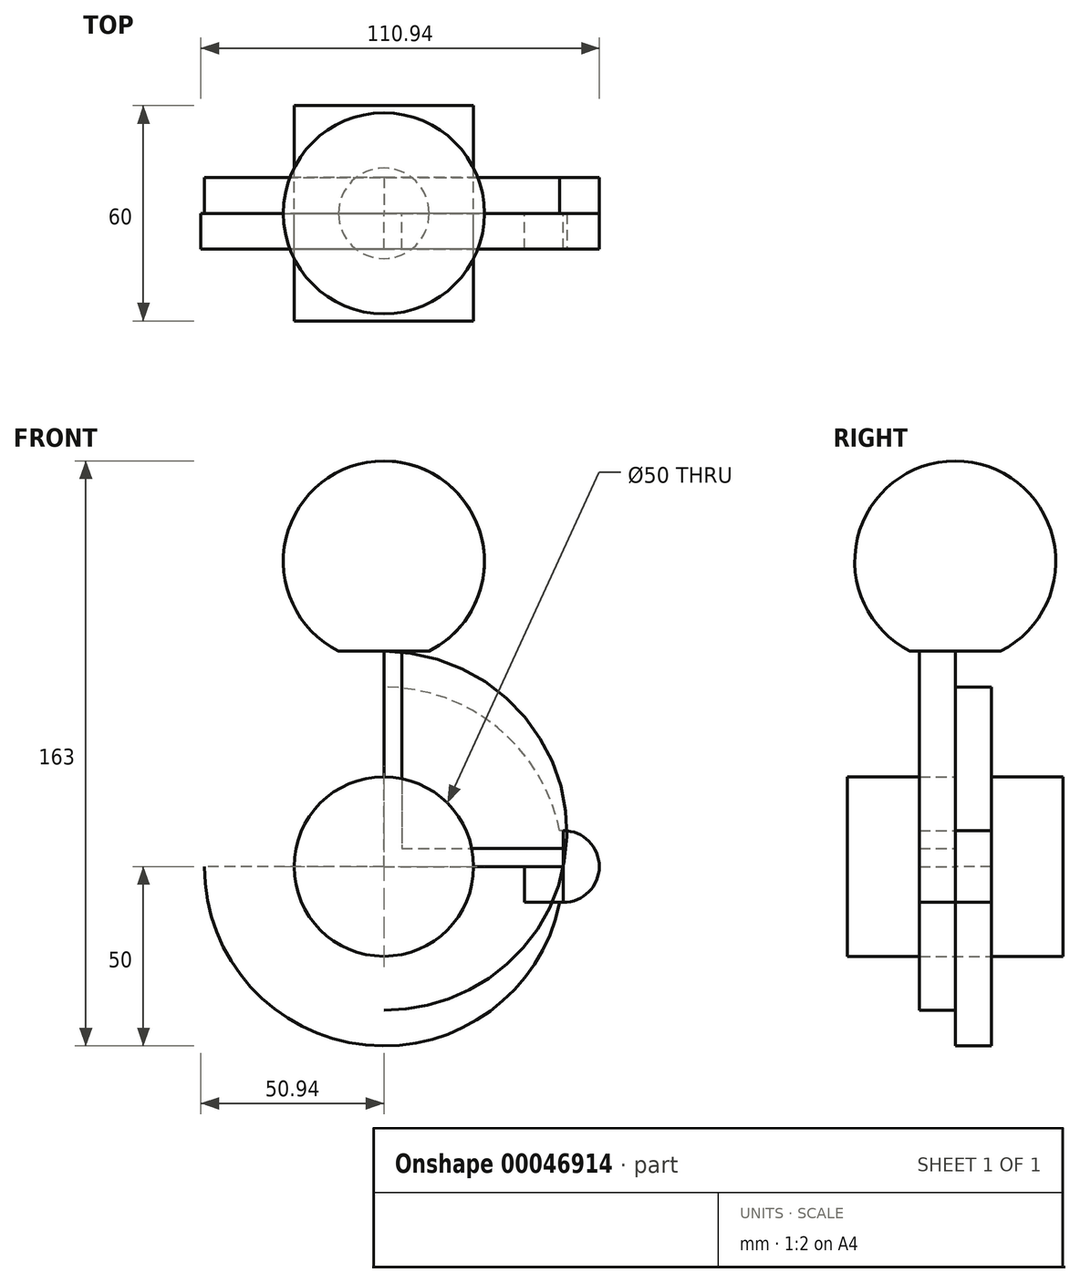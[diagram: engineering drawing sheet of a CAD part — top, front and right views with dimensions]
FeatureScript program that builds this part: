
annotation { "Feature Type Name" : "Feature", "Feature Type Description" : "" }
export const myFeature = defineFeature(function(context is Context, id is Id, definition is map)
    precondition{}
    {
        {
            var Q0;
            Q0=qCreatedBy(makeId("Front.planeOp"),FACE);
            var sketch = newSketch(context, id + "F0", { "sketchPlane" : qUnion([Q0])});
            skArc(sketch, "E0", {"start": v(49, 9.95) * mm, "mid": v(31.64, 38.71) * mm, "end": v(0, 50) * mm});
            skArc(sketch, "E1", {"start": v(49, -9.95) * mm, "mid": v(60, 0) * mm, "end": v(49, 9.95) * mm});
            skLineSegment(sketch, "E2.bottom", {"start": v(0, 0) * mm, "end": v(-50, 0) * mm});
            skLineSegment(sketch, "E2.left", {"start": v(0, 0) * mm, "end": v(0, 50) * mm});
            skArc(sketch, "E3.trimOffspring", {"start": v(-50, 0) * mm, "mid": v(-5, -49.75) * mm, "end": v(49, -9.95) * mm});
            skSolve(sketch);
        }
        {
            var Q0;
            Q0=makeQuery(id+"F0.imprint","IMPRINT",FACE,{"disambiguationData":[TD([[makeQuery(id+"F0.imprint","IMPRINT",EDGE,{"derivedFrom":sQuery(id+"F0.wireOp",EDGE,"E0")}),1.0]])]});
            extrude(context, id + "F1", {"entities" : qUnion([Q0]), "oppositeDirection" : true, "depth" : 10 * mm});
        }
        {
            var Q0;
            Q0=qCreatedBy(makeId("Front.planeOp"),FACE);
            var sketch = newSketch(context, id + "F2", { "sketchPlane" : qUnion([Q0])});
            skLineSegment(sketch, "E4", {"start": v(25, 43.3) * mm, "end": v(29.33, 50.8) * mm, "construction": true});
            skLineSegment(sketch, "E5", {"start": v(0, 50) * mm, "end": v(0, 60) * mm, "construction": true});
            skLineSegment(sketch, "E6", {"start": v(43.3, 25) * mm, "end": v(47.63, 27.5) * mm, "construction": true});
            skPoint(sketch, "E7", {"position": v(50, 0) * mm});
            skLineSegment(sketch, "E8", {"start": v(43.3, -25) * mm, "end": v(38.97, -22.5) * mm, "construction": true});
            skLineSegment(sketch, "E9", {"start": v(25, -43.3) * mm, "end": v(20.67, -35.8) * mm, "construction": true});
            skLineSegment(sketch, "E10", {"start": v(0, -50) * mm, "end": v(0, -40) * mm, "construction": true});
            skFitSpline(sketch, "E11", {"points": [v(0, 60) * mm, v(29.33, 50.8) * mm, v(47.63, 27.5) * mm, v(50, 0) * mm, v(38.97, -22.5) * mm, v(20.67, -35.8) * mm, v(0, -40) * mm], "startDerivative": vector(175.41, 0) * mm, "endDerivative": vector(-141.48, 0) * mm});
            skFitSpline(sketch, "E12.MirrorCS", {"points": [v(0, 60) * mm, v(-29.33, 50.8) * mm, v(-47.63, 27.5) * mm, v(-50, 0) * mm, v(-38.97, -22.5) * mm, v(-20.67, -35.8) * mm, v(0, -40) * mm], "startDerivative": vector(-175.41, 0) * mm, "endDerivative": vector(141.48, 0) * mm});
            skCircle(sketch, "E13", {"center": v(0, 0) * mm, "radius": 25 * mm});
            skSolve(sketch);
        }
        {
            var Q0;
            Q0 = qSketchRegion(id + "F2", true);
            extrude(context, id + "F3", {"entities" : qUnion([Q0]), "depth" : 10 * mm});
        }
        {
            var Q0;
            Q0=qCreatedBy(makeId("Front.planeOp"),FACE);
            var sketch = newSketch(context, id + "F4", { "sketchPlane" : qUnion([Q0])});
            skCircle(sketch, "E14", {"center": v(0, 0) * mm, "radius": 25 * mm});
            skSolve(sketch);
        }
        {
            var Q0;
            Q0 = qSketchRegion(id + "F4", true);
            extrude(context, id + "F5", {"entities" : qUnion([Q0]), "endBound" : BoundingType.SYMMETRIC, "depth" : 60 * mm, "hasSecondDirection" : true, "secondDirectionOppositeDirection" : true, "secondDirectionDepth" : 20 * mm});
        }
        {
            var Q0;
            Q0=makeQuery(id+"F1.opExtrude","CAP_FACE",FACE,{"disambiguationData":[OSD([sQuery(id+"F0.wireOp",EDGE,"E0"),sQuery(id+"F0.wireOp",EDGE,"E1")])],"isStart":true});
            var sketch = newSketch(context, id + "F6", { "sketchPlane" : qUnion([Q0])});
            skArc(sketch, "E15", {"start": v(50, -10) * mm, "mid": v(60, 0) * mm, "end": v(50, 10) * mm});
            skLineSegment(sketch, "E16", {"start": v(50, -10) * mm, "end": v(50, 10) * mm});
            skPoint(sketch, "E17.orphan", {"position": v(60, 0) * mm});
            skPoint(sketch, "E18.orphan", {"position": v(40, 0) * mm});
            skSolve(sketch);
        }
        {
            var Q0;
            Q0 = qSketchRegion(id + "F6", true);
            extrude(context, id + "F7", {"entities" : qUnion([Q0]), "depth" : 10 * mm});
        }
        {
            var Q0;
            Q0=makeQuery(id+"F7.opExtrude","CAP_FACE",FACE,{"disambiguationData":[OSD([sQuery(id+"F6.wireOp",EDGE,"E15"),sQuery(id+"F6.wireOp",EDGE,"E16")])],"isStart":true});
            var sketch = newSketch(context, id + "F8", { "sketchPlane" : qUnion([Q0])});
            skLineSegment(sketch, "E19.bottom", {"start": v(-50, 0) * mm, "end": v(-39.12, 0) * mm});
            skLineSegment(sketch, "E19.top", {"start": v(-50, -10) * mm, "end": v(-39.12, -10) * mm});
            skLineSegment(sketch, "E19.left", {"start": v(-50, 0) * mm, "end": v(-50, -10) * mm});
            skLineSegment(sketch, "E19.right", {"start": v(-39.12, 0) * mm, "end": v(-39.12, -10) * mm});
            skSolve(sketch);
        }
        {
            var Q0;
            Q0 = qSketchRegion(id + "F8", true);
            extrude(context, id + "F9", {"entities" : qUnion([Q0]), "oppositeDirection" : true, "depth" : 10 * mm});
        }
        {
            var Q0;
            Q0=qCreatedBy(makeId("Front.planeOp"),FACE);
            var sketch = newSketch(context, id + "F10", { "sketchPlane" : qUnion([Q0])});
            skLineSegment(sketch, "E20.bottom", {"start": v(0, 0) * mm, "end": v(50, 0) * mm});
            skLineSegment(sketch, "E20.top", {"start": v(5, 5) * mm, "end": v(50, 5) * mm});
            skLineSegment(sketch, "E20.left", {"start": v(0, 0) * mm, "end": v(0, 60) * mm});
            skLineSegment(sketch, "E20.right", {"start": v(50, 0) * mm, "end": v(50, 5) * mm});
            skLineSegment(sketch, "E21.bottom", {"start": v(0, 60) * mm, "end": v(5, 60) * mm});
            skLineSegment(sketch, "E21.right", {"start": v(5, 60) * mm, "end": v(5, 5) * mm});
            skSolve(sketch);
        }
        {
            var Q0;
            Q0 = qSketchRegion(id + "F10", true);
            extrude(context, id + "F11", {"entities" : qUnion([Q0]), "depth" : 10 * mm});
        }
        {
            var Q0;
            Q0=qCreatedBy(makeId("Front.planeOp"),FACE);
            var sketch = newSketch(context, id + "F12", { "sketchPlane" : qUnion([Q0])});
            skArc(sketch, "E22", {"start": v(12.6, 60) * mm, "mid": v(27.24, 91.48) * mm, "end": v(0, 113) * mm});
            skLineSegment(sketch, "E23", {"start": v(0, 60) * mm, "end": v(0, 113) * mm});
            skLineSegment(sketch, "E24", {"start": v(0, 60) * mm, "end": v(12.6, 60) * mm});
            skSolve(sketch);
        }
        {
            var Q0;
            Q0=makeQuery(id+"F12.imprint","IMPRINT",FACE,{"disambiguationData":[TD([[makeQuery(id+"F12.imprint","IMPRINT",EDGE,{"derivedFrom":sQuery(id+"F12.wireOp",EDGE,"E22")}),1.0]])]});
            var Q1;
            Q1=sQuery(id+"F12.wireOp",EDGE,"E23");
            revolve(context, id + "F13", {"entities" : qUnion([Q0]), "axis" : qUnion([Q1]), "revolveType" : RevolveType.FULL});
        }
    });
